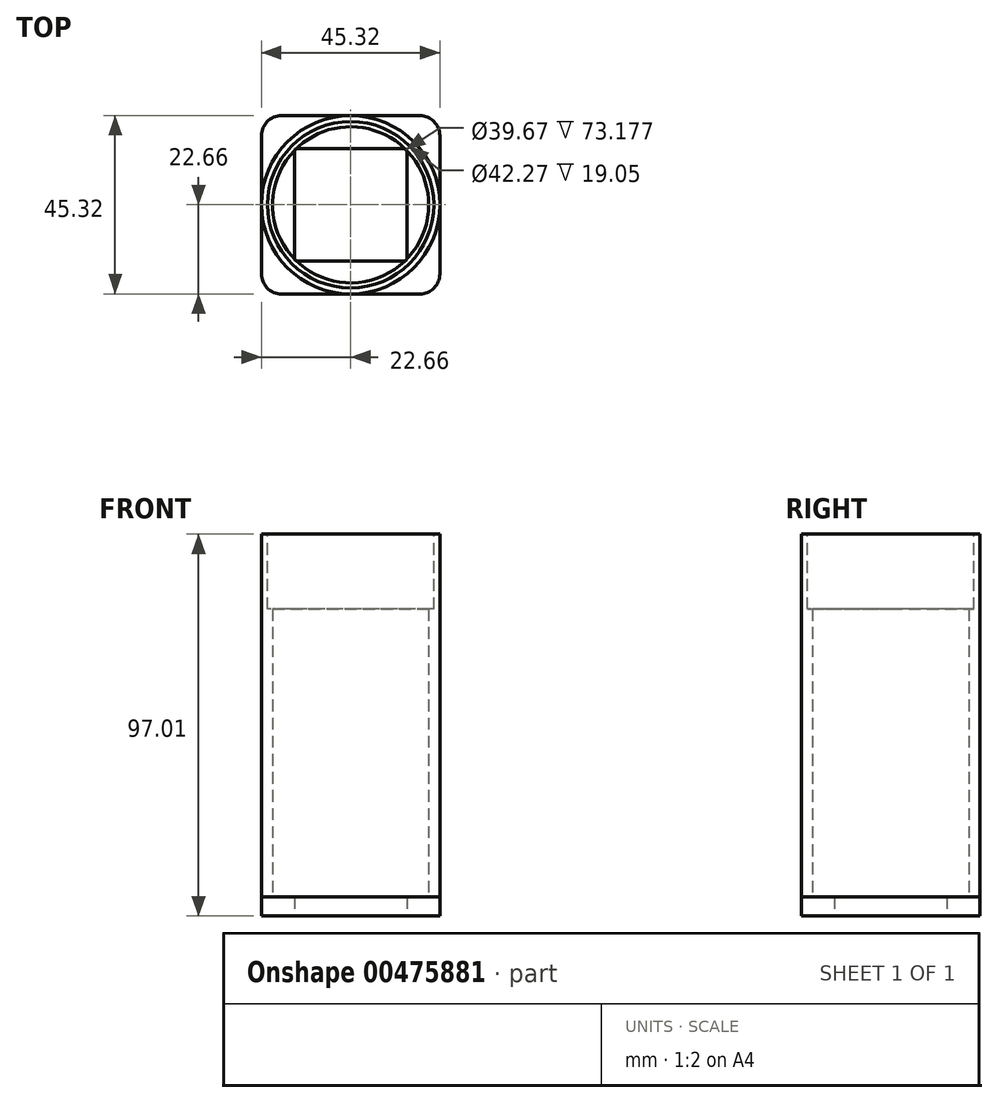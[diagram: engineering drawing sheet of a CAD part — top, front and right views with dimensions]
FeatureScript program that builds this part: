
annotation { "Feature Type Name" : "Feature", "Feature Type Description" : "" }
export const myFeature = defineFeature(function(context is Context, id is Id, definition is map)
    precondition{}
    {
        {
            var Q0;
            Q0=qCreatedBy(makeId("Top.planeOp"),FACE);
            var sketch = newSketch(context, id + "F0", { "sketchPlane" : qUnion([Q0])});
            skLineSegment(sketch, "E0.bottom", {"start": v(22.66, 22.66) * mm, "end": v(-22.66, 22.66) * mm});
            skLineSegment(sketch, "E0.top", {"start": v(22.66, -22.66) * mm, "end": v(-22.66, -22.66) * mm});
            skLineSegment(sketch, "E0.left", {"start": v(22.66, 22.66) * mm, "end": v(22.66, -22.66) * mm});
            skLineSegment(sketch, "E0.right", {"start": v(-22.66, 22.66) * mm, "end": v(-22.66, -22.66) * mm});
            skPoint(sketch, "E0.middle", {"position": v(0, 0) * mm});
            skSolve(sketch);
        }
        {
            var Q0;
            Q0 = qSketchRegion(id + "F0", true);
            extrude(context, id + "F1", {"entities" : qUnion([Q0]), "endBound" : BoundingType.SYMMETRIC, "depth" : 4.78 * mm});
        }
        {
            var Q0;
            Q0=makeQuery(id+"F1.opExtrude","CAP_FACE",FACE,{"disambiguationData":[OSD([sQuery(id+"F0.wireOp",EDGE,"E0.bottom"),sQuery(id+"F0.wireOp",EDGE,"E0.top"),sQuery(id+"F0.wireOp",EDGE,"E0.left"),sQuery(id+"F0.wireOp",EDGE,"E0.right")])],"isStart":false});
            var sketch = newSketch(context, id + "F2", { "sketchPlane" : qUnion([Q0])});
            skCircle(sketch, "E1", {"center": v(0, 0) * mm, "radius": 22.66 * mm});
            skCircle(sketch, "E2", {"center": v(0, 0) * mm, "radius": 19.84 * mm});
            skSolve(sketch);
        }
        {
            var Q0;
            Q0 = qSketchRegion(id + "F2", true);
            extrude(context, id + "F3", {"entities" : qUnion([Q0]), "operationType" : NewBodyOperationType.ADD, "depth" : 92.23 * mm});
        }
        {
            var Q0;
            Q0=makeQuery(id+"F1.opExtrude","CAP_FACE",FACE,{"disambiguationData":[OSD([sQuery(id+"F0.wireOp",EDGE,"E0.bottom"),sQuery(id+"F0.wireOp",EDGE,"E0.top"),sQuery(id+"F0.wireOp",EDGE,"E0.left"),sQuery(id+"F0.wireOp",EDGE,"E0.right")])],"isStart":true});
            var sketch = newSketch(context, id + "F4", { "sketchPlane" : qUnion([Q0])});
            skLineSegment(sketch, "E3.bottom", {"start": v(14.29, 14.29) * mm, "end": v(-14.29, 14.29) * mm});
            skLineSegment(sketch, "E3.top", {"start": v(14.29, -14.29) * mm, "end": v(-14.29, -14.29) * mm});
            skLineSegment(sketch, "E3.left", {"start": v(14.29, 14.29) * mm, "end": v(14.29, -14.29) * mm});
            skLineSegment(sketch, "E3.right", {"start": v(-14.29, 14.29) * mm, "end": v(-14.29, -14.29) * mm});
            skPoint(sketch, "E3.middle", {"position": v(0, 0) * mm});
            skSolve(sketch);
        }
        {
            var Q0;
            Q0 = qSketchRegion(id + "F4", true);
            var Q1;
            {var subQ0=sQuery(id+"F0.wireOp",EDGE,"E0.right");var subQ1=sQuery(id+"F0.wireOp",EDGE,"E0.top");var subQ2=makeQuery(id+"F1.opExtrude","CAP_FACE",FACE,{"disambiguationData":[OSD([sQuery(id+"F0.wireOp",EDGE,"E0.bottom"),subQ1,sQuery(id+"F0.wireOp",EDGE,"E0.left"),subQ0])],"isStart":false});Q1=makeQuery(id+"F3.boolean.opBoolean","SPLIT",FACE,{"disambiguationData":[TD([subQ2,makeQuery(id+"F1.opExtrude","SWEPT_FACE",FACE,{"disambiguationData":[OSD([subQ1])]}),makeQuery(id+"F1.opExtrude","SWEPT_FACE",FACE,{"disambiguationData":[OSD([subQ0])]}),makeQuery(id+"F3.opExtrude","SWEPT_FACE",FACE,{"disambiguationData":[OSD([sQuery(id+"F2.wireOp",EDGE,"E1")])]})])],"derivedFrom":subQ2});}
            extrude(context, id + "F5", {"entities" : qUnion([Q0]), "operationType" : NewBodyOperationType.REMOVE, "endBound" : BoundingType.UP_TO_SURFACE, "oppositeDirection" : true, "endBoundEntityFace" : qUnion([Q1]), "depth" : 25.4 * mm});
        }
        {
            var Q0;
            Q0=makeQuery(id+"F3.opExtrude","CAP_FACE",FACE,{"disambiguationData":[OSD([sQuery(id+"F2.wireOp",EDGE,"E1"),sQuery(id+"F2.wireOp",EDGE,"E2")])],"isStart":false});
            var sketch = newSketch(context, id + "F6", { "sketchPlane" : qUnion([Q0])});
            skCircle(sketch, "E4", {"center": v(0, 0) * mm, "radius": 21.13 * mm});
            skSolve(sketch);
        }
        {
            var Q0;
            Q0 = qSketchRegion(id + "F6", true);
            extrude(context, id + "F7", {"entities" : qUnion([Q0]), "operationType" : NewBodyOperationType.REMOVE, "oppositeDirection" : true, "depth" : 19.05 * mm});
        }
        {
            var Q0;
            Q0=makeQuery(id+"F1.opExtrude","SWEPT_EDGE",EDGE,{"disambiguationData":[OSD([sQuery(id+"F0.wireOp",EDGE,"E0.top"),sQuery(id+"F0.wireOp",EDGE,"E0.right")])]});
            var Q1;
            Q1=makeQuery(id+"F1.opExtrude","SWEPT_EDGE",EDGE,{"disambiguationData":[OSD([sQuery(id+"F0.wireOp",EDGE,"E0.bottom"),sQuery(id+"F0.wireOp",EDGE,"E0.right")])]});
            var Q2;
            Q2=makeQuery(id+"F1.opExtrude","SWEPT_EDGE",EDGE,{"disambiguationData":[OSD([sQuery(id+"F0.wireOp",EDGE,"E0.top"),sQuery(id+"F0.wireOp",EDGE,"E0.left")])]});
            var Q3;
            Q3=makeQuery(id+"F1.opExtrude","SWEPT_EDGE",EDGE,{"disambiguationData":[OSD([sQuery(id+"F0.wireOp",EDGE,"E0.bottom"),sQuery(id+"F0.wireOp",EDGE,"E0.left")])]});
            fillet(context, id + "F8", {"entities" : qUnion([Q0, Q1, Q2, Q3]), "radius" : 5.08 * mm, "tangentPropagation" : true, "allowEdgeOverflow" : false});
        }
    });
